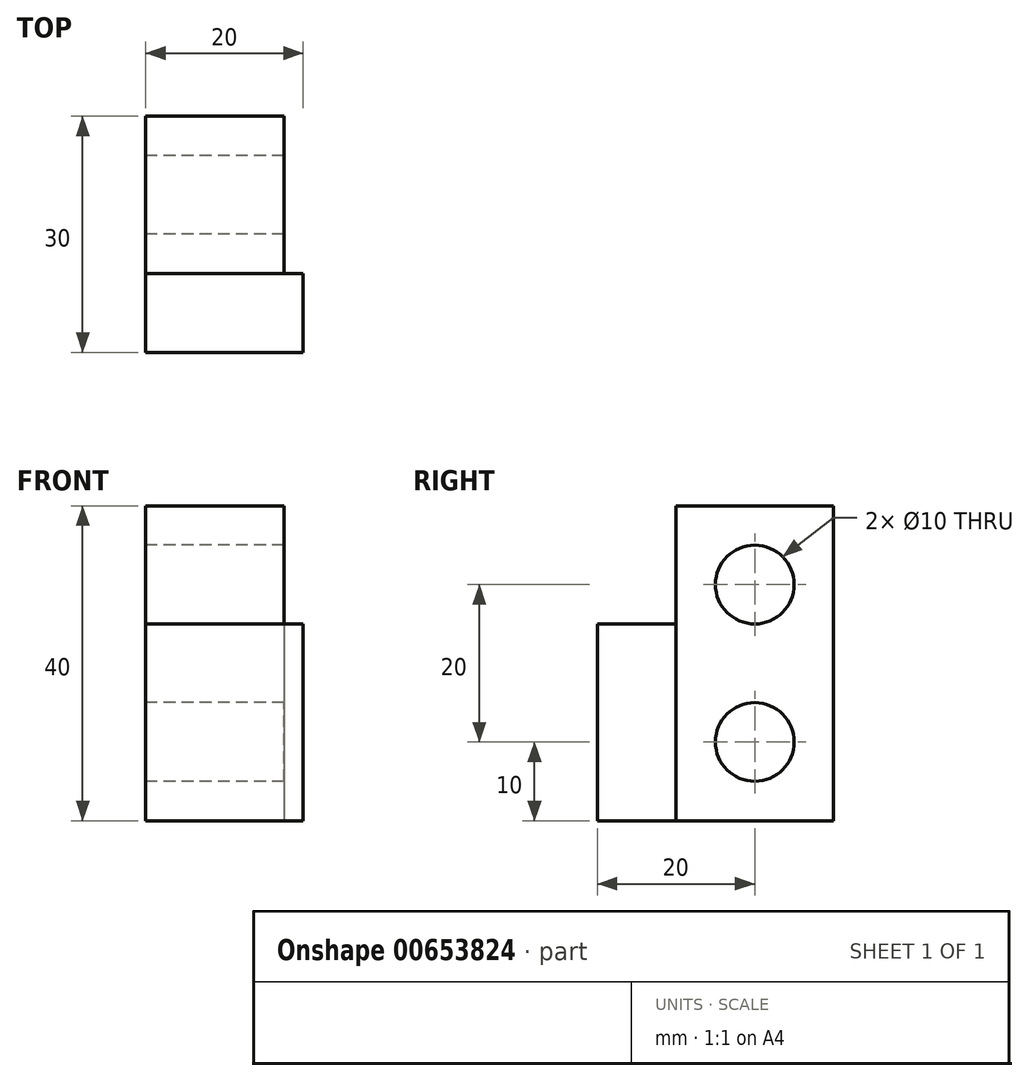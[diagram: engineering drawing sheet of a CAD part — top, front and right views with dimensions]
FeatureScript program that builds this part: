
annotation { "Feature Type Name" : "Feature", "Feature Type Description" : "" }
export const myFeature = defineFeature(function(context is Context, id is Id, definition is map)
    precondition{}
    {
        {
            var Q0;
            Q0=qCreatedBy(makeId("Right.planeOp"),FACE);
            var sketch = newSketch(context, id + "F0", { "sketchPlane" : qUnion([Q0])});
            skLineSegment(sketch, "E0.bottom", {"start": v(10, 20) * mm, "end": v(-10, 20) * mm});
            skLineSegment(sketch, "E0.top", {"start": v(10, -20) * mm, "end": v(-10, -20) * mm});
            skLineSegment(sketch, "E0.left", {"start": v(10, 20) * mm, "end": v(10, -20) * mm});
            skLineSegment(sketch, "E0.right", {"start": v(-10, 20) * mm, "end": v(-10, -20) * mm});
            skPoint(sketch, "E0.middle", {"position": v(0, 0) * mm});
            skLineSegment(sketch, "E1.bottom", {"start": v(-10, -20) * mm, "end": v(-20, -20) * mm});
            skLineSegment(sketch, "E1.top", {"start": v(-10, 5) * mm, "end": v(-20, 5) * mm});
            skLineSegment(sketch, "E1.left", {"start": v(-10, -20) * mm, "end": v(-10, 5) * mm});
            skLineSegment(sketch, "E1.right", {"start": v(-20, -20) * mm, "end": v(-20, 5) * mm});
            skCircle(sketch, "E2", {"center": v(0, -10) * mm, "radius": 5 * mm});
            skSolve(sketch);
        }
        {
            var Q0;
            Q0=makeQuery(id+"F0.imprint","IMPRINT",FACE,{"disambiguationData":[TD([[makeQuery(id+"F0.imprint","IMPRINT",EDGE,{"derivedFrom":sQuery(id+"F0.wireOp",EDGE,"E0.bottom")}),1.0]])]});
            extrude(context, id + "F1", {"entities" : qUnion([Q0]), "depth" : 17.55 * mm, "offsetDistance" : 25.4 * mm});
        }
        {
            var Q0;
            Q0=makeQuery(id+"F0.imprint","IMPRINT",FACE,{"disambiguationData":[TD([[makeQuery(id+"F0.imprint","IMPRINT",EDGE,{"derivedFrom":sQuery(id+"F0.wireOp",EDGE,"E1.bottom")}),-1.0]])]});
            extrude(context, id + "F2", {"entities" : qUnion([Q0]), "operationType" : NewBodyOperationType.ADD, "depth" : 20 * mm, "offsetDistance" : 25.4 * mm});
        }
        {
            var Q0;
            Q0=makeQuery(id+"F0.imprint","IMPRINT",FACE,{"disambiguationData":[TD([[makeQuery(id+"F0.imprint","IMPRINT",EDGE,{"derivedFrom":sQuery(id+"F0.wireOp",EDGE,"E0.bottom")}),1.0]])]});
            var sketch = newSketch(context, id + "F3", { "sketchPlane" : qUnion([Q0])});
            skCircle(sketch, "E3", {"center": v(0, 10) * mm, "radius": 5 * mm});
            skSolve(sketch);
        }
        {
            var Q0;
            Q0=makeQuery(id+"F3.imprint","IMPRINT",FACE,{"disambiguationData":[TD([[makeQuery(id+"F3.imprint","IMPRINT",EDGE,{"derivedFrom":sQuery(id+"F3.wireOp",EDGE,"E3")}),1.0]])]});
            var Q1;
            Q1=makeQuery(id+"F1.opExtrude","CAP_FACE",FACE,{"disambiguationData":[OSD([sQuery(id+"F0.wireOp",EDGE,"E0.bottom"),sQuery(id+"F0.wireOp",EDGE,"E0.top"),sQuery(id+"F0.wireOp",EDGE,"E0.left"),sQuery(id+"F0.wireOp",EDGE,"E0.right"),sQuery(id+"F0.wireOp",EDGE,"E1.left"),sQuery(id+"F0.wireOp",EDGE,"E2")])],"isStart":false});
            extrude(context, id + "F4", {"entities" : qUnion([Q0]), "operationType" : NewBodyOperationType.REMOVE, "endBound" : BoundingType.UP_TO_SURFACE, "depth" : 25.4 * mm, "endBoundEntityFace" : qUnion([Q1]), "offsetDistance" : 25.4 * mm});
        }
    });
